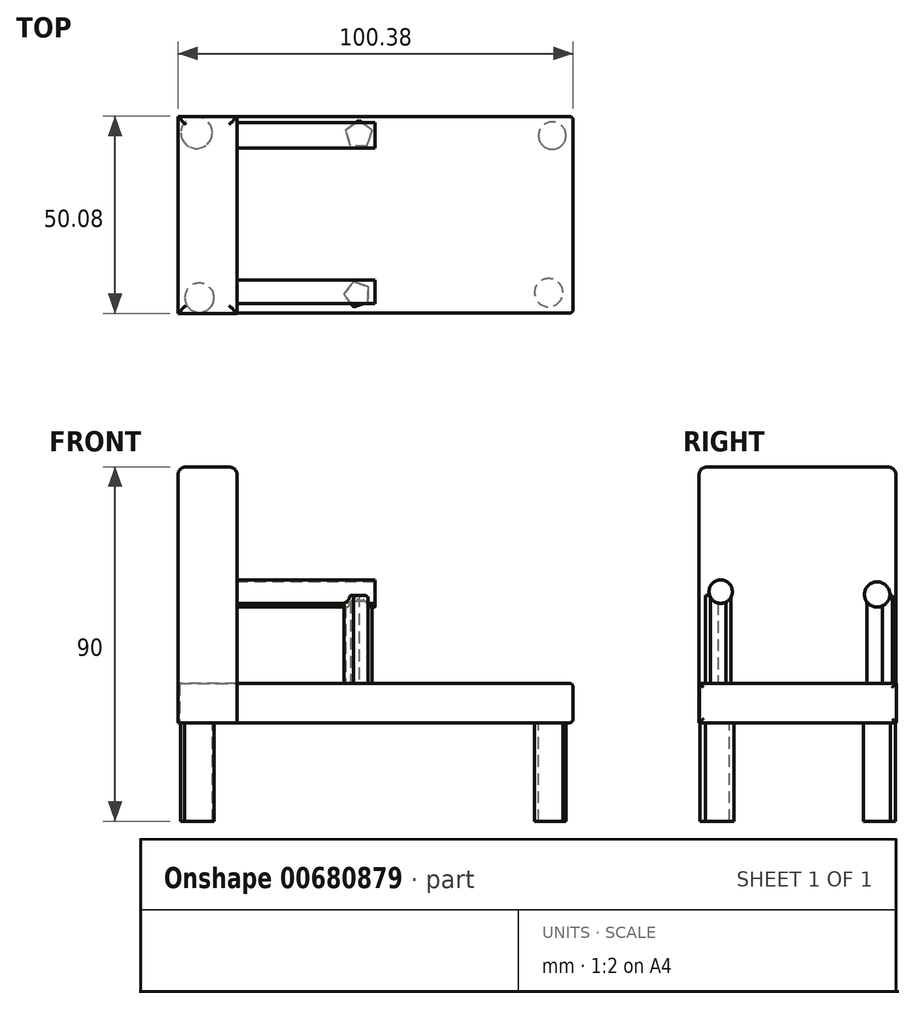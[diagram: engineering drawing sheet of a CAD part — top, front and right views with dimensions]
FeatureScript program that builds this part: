
annotation { "Feature Type Name" : "Feature", "Feature Type Description" : "" }
export const myFeature = defineFeature(function(context is Context, id is Id, definition is map)
    precondition{}
    {
        {
            var Q0;
            Q0=qCreatedBy(makeId("Top.planeOp"),FACE);
            var sketch = newSketch(context, id + "F0", { "sketchPlane" : qUnion([Q0])});
            skLineSegment(sketch, "E0.bottom", {"start": v(-42.17, 29.3) * mm, "end": v(57.83, 29.3) * mm});
            skLineSegment(sketch, "E0.top", {"start": v(-42.17, -20.7) * mm, "end": v(57.83, -20.7) * mm});
            skLineSegment(sketch, "E0.left", {"start": v(-42.17, 29.3) * mm, "end": v(-42.17, -20.7) * mm});
            skLineSegment(sketch, "E0.right", {"start": v(57.83, 29.3) * mm, "end": v(57.83, -20.7) * mm});
            skSolve(sketch);
        }
        {
            var Q0;
            Q0 = qSketchRegion(id + "F0", true);
            extrude(context, id + "F1", {"entities" : qUnion([Q0]), "depth" : 10 * mm, "offsetDistance" : 25 * mm});
        }
        {
            var Q0;
            Q0=makeQuery(id+"F1.opExtrude","CAP_FACE",FACE,{"disambiguationData":[OSD([sQuery(id+"F0.wireOp",EDGE,"E0.bottom"),sQuery(id+"F0.wireOp",EDGE,"E0.top"),sQuery(id+"F0.wireOp",EDGE,"E0.left"),sQuery(id+"F0.wireOp",EDGE,"E0.right")])],"isStart":true});
            var sketch = newSketch(context, id + "F2", { "sketchPlane" : qUnion([Q0])});
            skCircle(sketch, "E1", {"center": v(51.62, 15.51) * mm, "radius": 3.6 * mm});
            skCircle(sketch, "E2", {"center": v(52.53, -24.4) * mm, "radius": 3.49 * mm});
            skCircle(sketch, "E3", {"center": v(-37.1, 16.78) * mm, "radius": 3.72 * mm});
            skCircle(sketch, "E4", {"center": v(-37.83, -25.13) * mm, "radius": 4 * mm});
            skSolve(sketch);
        }
        {
            var Q0;
            Q0 = qSketchRegion(id + "F2", true);
            extrude(context, id + "F3", {"entities" : qUnion([Q0]), "operationType" : NewBodyOperationType.ADD, "depth" : 25 * mm, "offsetDistance" : 25 * mm});
        }
        {
            var Q0;
            Q0=qCreatedBy(makeId("Top.planeOp"),FACE);
            var sketch = newSketch(context, id + "F4", { "sketchPlane" : qUnion([Q0])});
            skLineSegment(sketch, "E5.bottom", {"start": v(-42.55, -20.78) * mm, "end": v(-27.55, -20.78) * mm});
            skLineSegment(sketch, "E5.top", {"start": v(-42.55, 29.22) * mm, "end": v(-27.55, 29.22) * mm});
            skLineSegment(sketch, "E5.left", {"start": v(-42.55, -20.78) * mm, "end": v(-42.55, 29.22) * mm});
            skLineSegment(sketch, "E5.right", {"start": v(-27.55, -20.78) * mm, "end": v(-27.55, 29.22) * mm});
            skSolve(sketch);
        }
        {
            var Q0;
            Q0 = qSketchRegion(id + "F4", true);
            extrude(context, id + "F5", {"entities" : qUnion([Q0]), "operationType" : NewBodyOperationType.ADD, "depth" : 65 * mm, "offsetDistance" : 25 * mm});
        }
        {
            var Q0;
            Q0=makeQuery(id+"F5.opExtrude","SWEPT_FACE",FACE,{"disambiguationData":[OSD([sQuery(id+"F4.wireOp",EDGE,"E5.right")])]});
            var sketch = newSketch(context, id + "F6", { "sketchPlane" : qUnion([Q0])});
            skCircle(sketch, "E6", {"center": v(-15.28, 33.32) * mm, "radius": 2.98 * mm});
            skCircle(sketch, "E7", {"center": v(24.46, 32.6) * mm, "radius": 3.21 * mm});
            skSolve(sketch);
        }
        {
            var Q0;
            Q0=makeQuery(id+"F6.imprint","IMPRINT",FACE,{"disambiguationData":[TD([[makeQuery(id+"F6.imprint","IMPRINT",EDGE,{"derivedFrom":sQuery(id+"F6.wireOp",EDGE,"E6")}),1.0]])]});
            var Q1;
            Q1=makeQuery(id+"F6.imprint","IMPRINT",FACE,{"disambiguationData":[TD([[makeQuery(id+"F6.imprint","IMPRINT",EDGE,{"derivedFrom":sQuery(id+"F6.wireOp",EDGE,"E7")}),1.0]])]});
            extrude(context, id + "F7", {"entities" : qUnion([Q0, Q1]), "operationType" : NewBodyOperationType.ADD, "depth" : 35 * mm, "offsetDistance" : 25 * mm});
        }
        {
            var Q0;
            Q0=makeQuery(id+"F1.opExtrude","CAP_FACE",FACE,{"disambiguationData":[OSD([sQuery(id+"F0.wireOp",EDGE,"E0.bottom"),sQuery(id+"F0.wireOp",EDGE,"E0.top"),sQuery(id+"F0.wireOp",EDGE,"E0.left"),sQuery(id+"F0.wireOp",EDGE,"E0.right")])],"isStart":false});
            var sketch = newSketch(context, id + "F8", { "sketchPlane" : qUnion([Q0])});
            skCircle(sketch, "E8.cCircle", {"center": v(3.02, -15.94) * mm, "radius": 2.72 * mm, "construction": true});
            skLineSegment(sketch, "E8.0", {"start": v(5.74, -13.96) * mm, "end": v(5.74, -17.91) * mm});
            skLineSegment(sketch, "E8.1", {"start": v(5.74, -17.91) * mm, "end": v(1.98, -19.14) * mm});
            skLineSegment(sketch, "E8.2", {"start": v(1.98, -19.14) * mm, "end": v(-0.34, -15.94) * mm});
            skLineSegment(sketch, "E8.3", {"start": v(-0.34, -15.94) * mm, "end": v(1.98, -12.74) * mm});
            skLineSegment(sketch, "E8.4", {"start": v(1.98, -12.74) * mm, "end": v(5.74, -13.96) * mm});
            skPoint(sketch, "E8.0.midPoint", {"position": v(5.74, -15.94) * mm});
            skCircle(sketch, "E9.cCircle", {"center": v(3.38, 24.7) * mm, "radius": 2.9 * mm, "construction": true});
            skLineSegment(sketch, "E9.0", {"start": v(5.5, 21.8) * mm, "end": v(1.27, 21.8) * mm});
            skLineSegment(sketch, "E9.1", {"start": v(1.27, 21.8) * mm, "end": v(-0.03, 25.82) * mm});
            skLineSegment(sketch, "E9.2", {"start": v(-0.03, 25.82) * mm, "end": v(3.38, 28.3) * mm});
            skLineSegment(sketch, "E9.3", {"start": v(3.38, 28.3) * mm, "end": v(6.8, 25.82) * mm});
            skLineSegment(sketch, "E9.4", {"start": v(6.8, 25.82) * mm, "end": v(5.5, 21.8) * mm});
            skPoint(sketch, "E9.0.midPoint", {"position": v(3.38, 21.8) * mm});
            skSolve(sketch);
        }
        {
            var Q0;
            Q0 = qSketchRegion(id + "F8", true);
            extrude(context, id + "F9", {"entities" : qUnion([Q0]), "operationType" : NewBodyOperationType.ADD, "depth" : 22.4 * mm, "offsetDistance" : 25 * mm});
        }
        {
            var Q0;
            Q0=makeQuery(id+"F5.opExtrude","CAP_FACE",FACE,{"disambiguationData":[OSD([sQuery(id+"F4.wireOp",EDGE,"E5.bottom"),sQuery(id+"F4.wireOp",EDGE,"E5.top"),sQuery(id+"F4.wireOp",EDGE,"E5.left"),sQuery(id+"F4.wireOp",EDGE,"E5.right")])],"isStart":false});
            fillet(context, id + "F10", {"entities" : qUnion([Q0]), "radius" : 2 * mm, "tangentPropagation" : true, "allowEdgeOverflow" : false});
        }
        {
            var Q0;
            Q0=makeQuery(id+"F1.opExtrude","SWEPT_FACE",FACE,{"disambiguationData":[OSD([sQuery(id+"F0.wireOp",EDGE,"E0.right")])]});
            fillet(context, id + "F11", {"entities" : qUnion([Q0]), "radius" : 1 * mm, "tangentPropagation" : true, "allowEdgeOverflow" : false});
        }
    });
